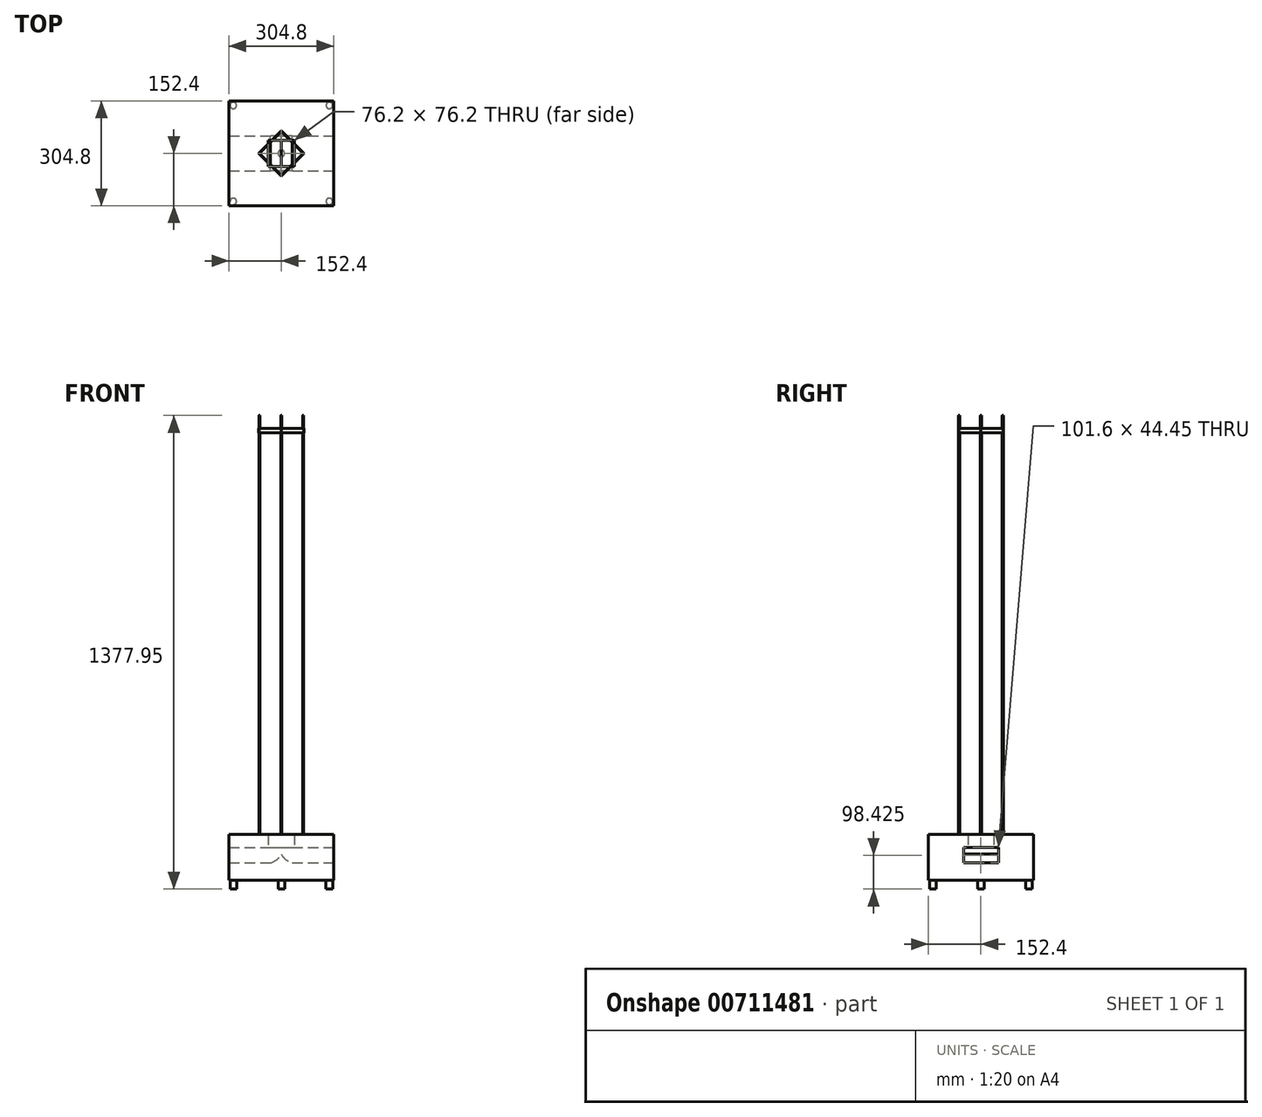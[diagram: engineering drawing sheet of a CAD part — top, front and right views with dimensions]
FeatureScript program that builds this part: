
annotation { "Feature Type Name" : "Feature", "Feature Type Description" : "" }
export const myFeature = defineFeature(function(context is Context, id is Id, definition is map)
    precondition{}
    {
        {
            var Q0;
            Q0=qCreatedBy(makeId("Top.planeOp"),FACE);
            var sketch = newSketch(context, id + "F0", { "sketchPlane" : qUnion([Q0])});
            skLineSegment(sketch, "E0", {"start": v(0, 0) * mm, "end": v(152.4, 0) * mm, "construction": true});
            skLineSegment(sketch, "E1", {"start": v(0, 0) * mm, "end": v(-152.4, 0) * mm, "construction": true});
            skLineSegment(sketch, "E2", {"start": v(-152.4, 0) * mm, "end": v(-152.4, 152.4) * mm});
            skLineSegment(sketch, "E3", {"start": v(-152.4, 152.4) * mm, "end": v(152.4, 152.4) * mm});
            skLineSegment(sketch, "E4", {"start": v(152.4, 152.4) * mm, "end": v(152.4, 0) * mm});
            skLineSegment(sketch, "E5", {"start": v(-152.4, 0) * mm, "end": v(-152.4, -152.4) * mm});
            skLineSegment(sketch, "E6", {"start": v(-152.4, -152.4) * mm, "end": v(152.4, -152.4) * mm});
            skLineSegment(sketch, "E7", {"start": v(152.4, 0) * mm, "end": v(152.4, -152.4) * mm});
            skLineSegment(sketch, "E8", {"start": v(0, 0) * mm, "end": v(0, 38.1) * mm, "construction": true});
            skLineSegment(sketch, "E9", {"start": v(0, 38.1) * mm, "end": v(38.1, 38.1) * mm});
            skLineSegment(sketch, "E10", {"start": v(38.1, 38.1) * mm, "end": v(38.1, -38.1) * mm});
            skLineSegment(sketch, "E11", {"start": v(38.1, -38.1) * mm, "end": v(-38.1, -38.1) * mm});
            skLineSegment(sketch, "E12", {"start": v(-38.1, -38.1) * mm, "end": v(-38.1, 38.1) * mm});
            skLineSegment(sketch, "E13", {"start": v(-38.1, 38.1) * mm, "end": v(0, 38.1) * mm});
            skSolve(sketch);
        }
        {
            var Q0;
            Q0 = qSketchRegion(id + "F0", true);
            extrude(context, id + "F1", {"entities" : qUnion([Q0]), "depth" : 38.1 * mm, "offsetDistance" : 25.4 * mm});
        }
        {
            var Q0;
            Q0=qCreatedBy(makeId("Front.planeOp"),FACE);
            var sketch = newSketch(context, id + "F2", { "sketchPlane" : qUnion([Q0])});
            skLineSegment(sketch, "E14", {"start": v(0, 0) * mm, "end": v(-38.1, 0) * mm, "construction": true});
            skLineSegment(sketch, "E15", {"start": v(0, 0) * mm, "end": v(0, -19.05) * mm, "construction": true});
            skLineSegment(sketch, "E16", {"start": v(0, -19.05) * mm, "end": v(0, -44.45) * mm});
            skArc(sketch, "E17", {"start": v(-31.75, -44.45) * mm, "mid": v(-13.22, -35.07) * mm, "end": v(0, -19.05) * mm});
            skLineSegment(sketch, "E18", {"start": v(-31.75, -44.45) * mm, "end": v(0, -44.45) * mm});
            skLineSegment(sketch, "E19", {"start": v(0, -44.45) * mm, "end": v(31.75, -44.45) * mm});
            skArc(sketch, "E20", {"start": v(0, -19.05) * mm, "mid": v(13.22, -35.07) * mm, "end": v(31.75, -44.45) * mm});
            skLineSegment(sketch, "E21", {"start": v(31.75, -44.45) * mm, "end": v(152.4, -44.45) * mm});
            skLineSegment(sketch, "E22", {"start": v(-31.75, -44.45) * mm, "end": v(-152.4, -44.45) * mm});
            skLineSegment(sketch, "E23", {"start": v(-152.4, -44.45) * mm, "end": v(-152.4, -95.25) * mm});
            skLineSegment(sketch, "E24", {"start": v(-152.4, -95.25) * mm, "end": v(152.4, -95.25) * mm});
            skLineSegment(sketch, "E25", {"start": v(152.4, -95.25) * mm, "end": v(152.4, -44.45) * mm});
            skSolve(sketch);
        }
        {
            var Q0;
            Q0 = qSketchRegion(id + "F2", true);
            extrude(context, id + "F3", {"entities" : qUnion([Q0]), "endBound" : BoundingType.SYMMETRIC, "depth" : 304.8 * mm, "offsetDistance" : 25.4 * mm});
        }
        {
            var Q0;
            Q0=makeQuery(id+"F3.opExtrude","SWEPT_FACE",FACE,{"disambiguationData":[OSD([sQuery(id+"F2.wireOp",EDGE,"E22")])]});
            var sketch = newSketch(context, id + "F4", { "sketchPlane" : qUnion([Q0])});
            skLineSegment(sketch, "E26", {"start": v(0, 0) * mm, "end": v(0, 50.8) * mm, "construction": true});
            skLineSegment(sketch, "E27", {"start": v(0, 0) * mm, "end": v(0, -50.8) * mm, "construction": true});
            skLineSegment(sketch, "E28", {"start": v(0, -50.8) * mm, "end": v(152.4, -50.8) * mm});
            skLineSegment(sketch, "E29", {"start": v(152.4, -50.8) * mm, "end": v(152.4, -152.4) * mm});
            skLineSegment(sketch, "E30", {"start": v(152.4, -152.4) * mm, "end": v(-152.4, -152.4) * mm});
            skLineSegment(sketch, "E31", {"start": v(-152.4, -152.4) * mm, "end": v(-152.4, -50.8) * mm});
            skLineSegment(sketch, "E32", {"start": v(-152.4, -50.8) * mm, "end": v(0, -50.8) * mm});
            skLineSegment(sketch, "E33", {"start": v(0, 50.8) * mm, "end": v(152.4, 50.8) * mm});
            skLineSegment(sketch, "E34", {"start": v(152.4, 50.8) * mm, "end": v(152.4, 152.4) * mm});
            skLineSegment(sketch, "E35", {"start": v(152.4, 152.4) * mm, "end": v(-152.4, 152.4) * mm});
            skLineSegment(sketch, "E36", {"start": v(-152.4, 152.4) * mm, "end": v(-152.4, 50.8) * mm});
            skLineSegment(sketch, "E37", {"start": v(-152.4, 50.8) * mm, "end": v(0, 50.8) * mm});
            skSolve(sketch);
        }
        {
            var Q0;
            Q0 = qSketchRegion(id + "F4", true);
            extrude(context, id + "F5", {"entities" : qUnion([Q0]), "operationType" : NewBodyOperationType.ADD, "depth" : 44.45 * mm, "offsetDistance" : 25.4 * mm});
        }
        {
            var Q0;
            Q0=makeQuery(id+"F3.opExtrude","SWEPT_FACE",FACE,{"disambiguationData":[OSD([sQuery(id+"F2.wireOp",EDGE,"E24")])]});
            var sketch = newSketch(context, id + "F6", { "sketchPlane" : qUnion([Q0])});
            skLineSegment(sketch, "E38", {"start": v(0, 0) * mm, "end": v(0, 139.7) * mm, "construction": true});
            skLineSegment(sketch, "E39", {"start": v(0, 139.7) * mm, "end": v(-139.7, 139.7) * mm, "construction": true});
            skLineSegment(sketch, "E40", {"start": v(-139.7, 139.7) * mm, "end": v(-139.7, -139.7) * mm, "construction": true});
            skLineSegment(sketch, "E41", {"start": v(-139.7, -139.7) * mm, "end": v(139.7, -139.7) * mm, "construction": true});
            skLineSegment(sketch, "E42", {"start": v(139.7, -139.7) * mm, "end": v(139.7, 139.7) * mm, "construction": true});
            skLineSegment(sketch, "E43", {"start": v(139.7, 139.7) * mm, "end": v(0, 139.7) * mm, "construction": true});
            skCircle(sketch, "E44", {"center": v(-139.7, 139.7) * mm, "radius": 9.53 * mm});
            skCircle(sketch, "E45", {"center": v(139.7, 139.7) * mm, "radius": 9.53 * mm});
            skCircle(sketch, "E46", {"center": v(139.7, -139.7) * mm, "radius": 9.53 * mm});
            skCircle(sketch, "E47", {"center": v(-139.7, -139.7) * mm, "radius": 9.53 * mm});
            skCircle(sketch, "E48", {"center": v(0, 0) * mm, "radius": 9.52 * mm});
            skSolve(sketch);
        }
        {
            var Q0;
            Q0 = qSketchRegion(id + "F6", true);
            extrude(context, id + "F7", {"entities" : qUnion([Q0]), "operationType" : NewBodyOperationType.ADD, "depth" : 25.4 * mm, "offsetDistance" : 25.4 * mm});
        }
        {
            var Q0;
            Q0=makeQuery(id+"F1.opExtrude","CAP_FACE",FACE,{"disambiguationData":[OSD([sQuery(id+"F0.wireOp",EDGE,"E2"),sQuery(id+"F0.wireOp",EDGE,"E3"),sQuery(id+"F0.wireOp",EDGE,"E4"),sQuery(id+"F0.wireOp",EDGE,"E5"),sQuery(id+"F0.wireOp",EDGE,"E6"),sQuery(id+"F0.wireOp",EDGE,"E7"),sQuery(id+"F0.wireOp",EDGE,"E9"),sQuery(id+"F0.wireOp",EDGE,"E10"),sQuery(id+"F0.wireOp",EDGE,"E11"),sQuery(id+"F0.wireOp",EDGE,"E12"),sQuery(id+"F0.wireOp",EDGE,"E13")])],"isStart":false});
            var sketch = newSketch(context, id + "F8", { "sketchPlane" : qUnion([Q0])});
            skLineSegment(sketch, "E49", {"start": v(0, 0) * mm, "end": v(0, 63.5) * mm, "construction": true});
            skPoint(sketch, "E49.endSnap0", {"position": v(0, 38.1) * mm});
            skLineSegment(sketch, "E50", {"start": v(0, 0) * mm, "end": v(0, -63.5) * mm, "construction": true});
            skLineSegment(sketch, "E51", {"start": v(0, 0) * mm, "end": v(63.5, 0) * mm, "construction": true});
            skPoint(sketch, "E51.endSnap0", {"position": v(38.1, 0) * mm});
            skLineSegment(sketch, "E52", {"start": v(0, 0) * mm, "end": v(-63.5, 0) * mm, "construction": true});
            skCircle(sketch, "E53", {"center": v(0, 63.5) * mm, "radius": 1.59 * mm});
            skCircle(sketch, "E54", {"center": v(63.5, 0) * mm, "radius": 1.59 * mm});
            skCircle(sketch, "E55", {"center": v(-63.5, 0) * mm, "radius": 1.59 * mm});
            skCircle(sketch, "E56", {"center": v(0, -63.5) * mm, "radius": 1.59 * mm});
            skSolve(sketch);
        }
        {
            var Q0;
            Q0 = qSketchRegion(id + "F8", true);
            extrude(context, id + "F9", {"entities" : qUnion([Q0]), "operationType" : NewBodyOperationType.ADD, "depth" : 1219.2 * mm, "offsetDistance" : 25.4 * mm});
        }
        {
            var Q0;
            Q0=makeQuery(id+"F1.opExtrude","CAP_FACE",FACE,{"disambiguationData":[OSD([sQuery(id+"F0.wireOp",EDGE,"E2"),sQuery(id+"F0.wireOp",EDGE,"E3"),sQuery(id+"F0.wireOp",EDGE,"E4"),sQuery(id+"F0.wireOp",EDGE,"E5"),sQuery(id+"F0.wireOp",EDGE,"E6"),sQuery(id+"F0.wireOp",EDGE,"E7"),sQuery(id+"F0.wireOp",EDGE,"E9"),sQuery(id+"F0.wireOp",EDGE,"E10"),sQuery(id+"F0.wireOp",EDGE,"E11"),sQuery(id+"F0.wireOp",EDGE,"E12"),sQuery(id+"F0.wireOp",EDGE,"E13")])],"isStart":true});
            cPlane(context, id + "F10", {"entities" : qUnion([Q0]), "cplaneType" : CPlaneType.OFFSET, "offset" : 1219.2 * mm, "oppositeDirection" : true, "width" : 152.4 * mm, "height" : 152.4 * mm});
        }
        {
            var Q0;
            Q0=qCreatedBy(id+"F10.planeOp",FACE);
            var sketch = newSketch(context, id + "F11", { "sketchPlane" : qUnion([Q0])});
            skLineSegment(sketch, "E57", {"start": v(0, 0) * mm, "end": v(0, -63.5) * mm, "construction": true});
            skLineSegment(sketch, "E58", {"start": v(0, 0) * mm, "end": v(63.5, 0) * mm, "construction": true});
            skLineSegment(sketch, "E59", {"start": v(0, 0) * mm, "end": v(0, 63.5) * mm, "construction": true});
            skLineSegment(sketch, "E60", {"start": v(0, 0) * mm, "end": v(-63.5, 0) * mm, "construction": true});
            skLineSegment(sketch, "E61", {"start": v(-63.5, 0) * mm, "end": v(0, -63.5) * mm});
            skLineSegment(sketch, "E62", {"start": v(63.5, 0) * mm, "end": v(0, -63.5) * mm});
            skLineSegment(sketch, "E63", {"start": v(63.5, 0) * mm, "end": v(0, 63.5) * mm});
            skLineSegment(sketch, "E64", {"start": v(-63.5, 0) * mm, "end": v(0, 63.5) * mm});
            skLineSegment(sketch, "E65", {"start": v(0, -63.5) * mm, "end": v(1.12, -64.62) * mm});
            skLineSegment(sketch, "E66", {"start": v(1.12, -64.62) * mm, "end": v(64.62, -1.12) * mm});
            skLineSegment(sketch, "E67", {"start": v(64.62, -1.12) * mm, "end": v(65.75, 0) * mm});
            skLineSegment(sketch, "E68", {"start": v(65.75, 0) * mm, "end": v(1.12, 64.62) * mm});
            skLineSegment(sketch, "E69", {"start": v(1.12, 64.62) * mm, "end": v(0, 63.5) * mm, "construction": true});
            skLineSegment(sketch, "E70", {"start": v(1.12, 64.62) * mm, "end": v(0, 65.75) * mm});
            skLineSegment(sketch, "E71", {"start": v(1.12, -64.62) * mm, "end": v(0, -65.75) * mm});
            skLineSegment(sketch, "E72", {"start": v(0, -65.75) * mm, "end": v(-64.62, -1.12) * mm});
            skLineSegment(sketch, "E73", {"start": v(-64.62, -1.12) * mm, "end": v(-63.5, 0) * mm, "construction": true});
            skLineSegment(sketch, "E74", {"start": v(-64.62, -1.12) * mm, "end": v(-65.75, 0) * mm});
            skLineSegment(sketch, "E75", {"start": v(-65.75, 0) * mm, "end": v(0, 65.75) * mm});
            skSolve(sketch);
        }
        {
            var Q0;
            Q0 = qSketchRegion(id + "F11", true);
            extrude(context, id + "F12", {"entities" : qUnion([Q0]), "operationType" : NewBodyOperationType.ADD, "depth" : 12.7 * mm, "offsetDistance" : 25.4 * mm});
        }
    });
